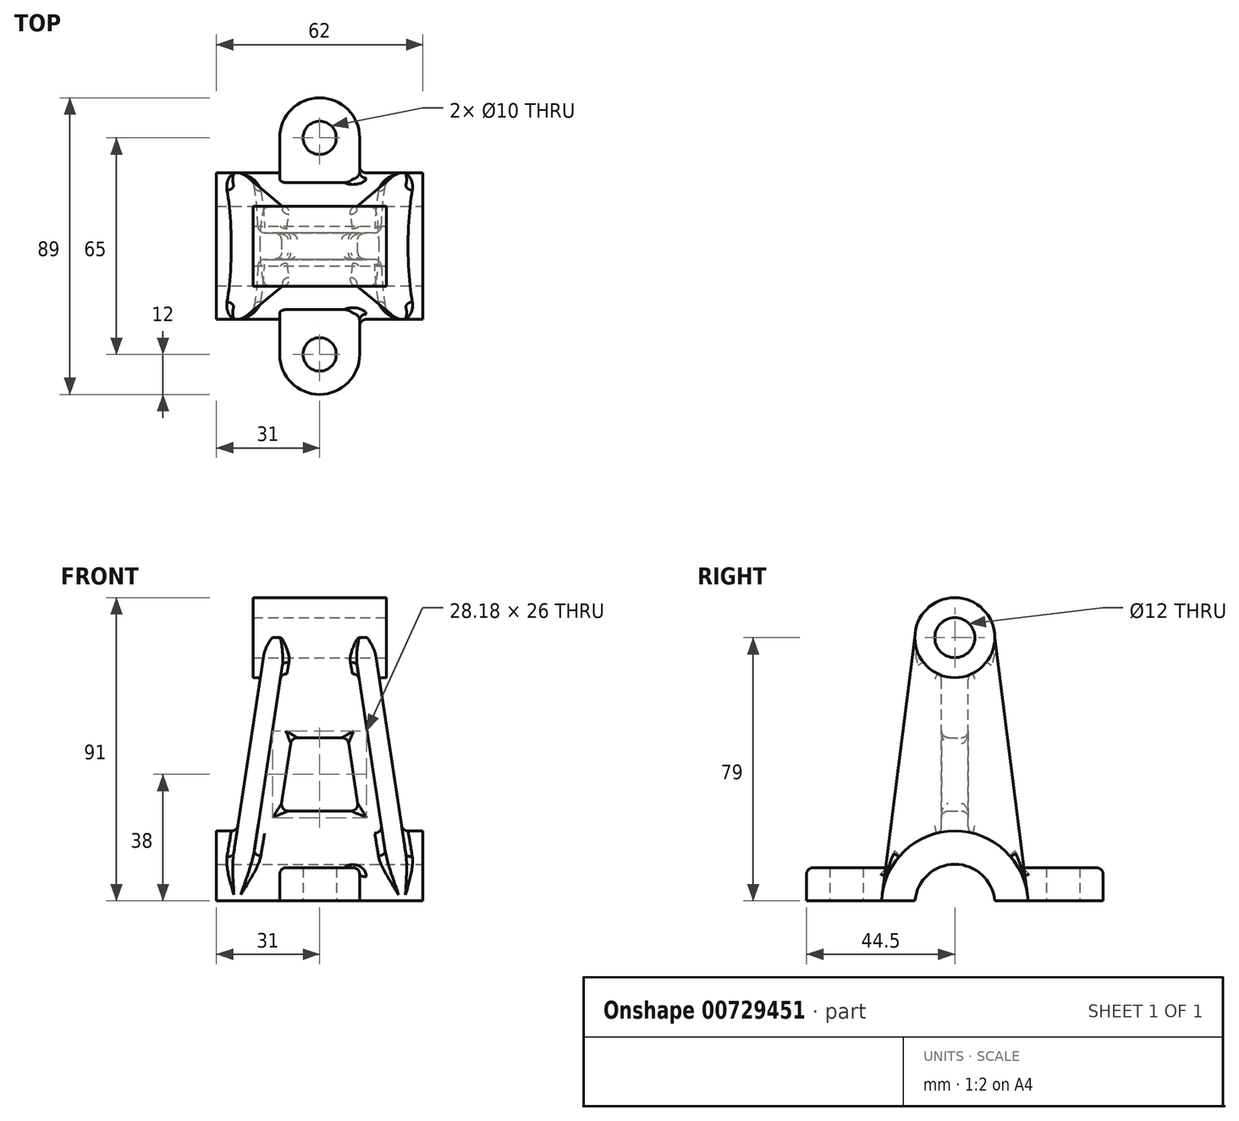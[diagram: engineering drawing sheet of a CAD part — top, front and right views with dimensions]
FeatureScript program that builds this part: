
annotation { "Feature Type Name" : "Feature", "Feature Type Description" : "" }
export const myFeature = defineFeature(function(context is Context, id is Id, definition is map)
    precondition{}
    {
        {
            var Q0;
            Q0=qCreatedBy(makeId("Right.planeOp"),FACE);
            var sketch = newSketch(context, id + "F0", { "sketchPlane" : qUnion([Q0])});
            skArc(sketch, "E0", {"start": v(21.98, 1) * mm, "mid": v(0, 22) * mm, "end": v(-21.98, 1) * mm});
            skArc(sketch, "E1", {"start": v(11.96, 1) * mm, "mid": v(0, 12) * mm, "end": v(-11.96, 1) * mm});
            skLineSegment(sketch, "E2", {"start": v(0, 0) * mm, "end": v(36.01, 0) * mm, "construction": true});
            skLineSegment(sketch, "E3", {"start": v(-21.98, 1) * mm, "end": v(21.98, 1) * mm});
            skSolve(sketch);
        }
        {
            var Q0;
            Q0 = qSketchRegion(id + "F0", true);
            extrude(context, id + "F1", {"entities" : qUnion([Q0]), "depth" : 62 * mm, "offsetDistance" : 25 * mm, "symmetric" : true});
        }
        {
            var Q0;
            Q0=qCreatedBy(makeId("Right.planeOp"),FACE);
            var sketch = newSketch(context, id + "F2", { "sketchPlane" : qUnion([Q0])});
            skLineSegment(sketch, "E4", {"start": v(0, 0) * mm, "end": v(0, 80) * mm, "construction": true});
            skCircle(sketch, "E5", {"center": v(0, 80) * mm, "radius": 6 * mm});
            skCircle(sketch, "E6", {"center": v(0, 80) * mm, "radius": 12 * mm});
            skSolve(sketch);
        }
        {
            var Q0;
            Q0 = qSketchRegion(id + "F2", true);
            var Q1;
            Q1=makeQuery(id+"F2.imprint","IMPRINT",FACE,{"disambiguationData":[TD([[makeQuery(id+"F2.imprint","IMPRINT",EDGE,{"derivedFrom":sQuery(id+"F2.wireOp",EDGE,"E5")}),1.0]])]});
            extrude(context, id + "F3", {"entities" : qUnion([Q0, Q1]), "depth" : 40 * mm, "offsetDistance" : 25 * mm, "symmetric" : true});
        }
        {
            var Q0;
            Q0=qCreatedBy(makeId("Front.planeOp"),FACE);
            var sketch = newSketch(context, id + "F4", { "sketchPlane" : qUnion([Q0])});
            skLineSegment(sketch, "E7", {"start": v(0, 0) * mm, "end": v(0, 29.66) * mm, "construction": true});
            skLineSegment(sketch, "E8", {"start": v(-16, 80) * mm, "end": v(16, 80) * mm});
            skLineSegment(sketch, "E9.0", {"start": v(28, 1) * mm, "end": v(-28, 1) * mm});
            skLineSegment(sketch, "E10", {"start": v(16, 80) * mm, "end": v(28, 1) * mm});
            skLineSegment(sketch, "E11.MirrorCS", {"start": v(-16, 80) * mm, "end": v(-28, 1) * mm});
            skLineSegment(sketch, "E12", {"start": v(-24.81, 22) * mm, "end": v(24.81, 22) * mm});
            skLineSegment(sketch, "E13.0", {"start": v(8.42, 50) * mm, "end": v(11.76, 28) * mm});
            skLineSegment(sketch, "E14.MirrorCS", {"start": v(-8.42, 50) * mm, "end": v(-11.76, 28) * mm});
            skLineSegment(sketch, "E15.trimOffspring", {"start": v(-8.42, 50) * mm, "end": v(8.42, 50) * mm});
            skLineSegment(sketch, "E16.trimOffspring", {"start": v(-11.76, 28) * mm, "end": v(11.76, 28) * mm});
            skPoint(sketch, "E17.orphan", {"position": v(-31, 1) * mm});
            skPoint(sketch, "E18.orphan", {"position": v(31, 1) * mm});
            skLineSegment(sketch, "E19", {"start": v(9.93, 80) * mm, "end": v(21.93, 1) * mm});
            skLineSegment(sketch, "E20.MirrorCS", {"start": v(-9.93, 80) * mm, "end": v(-21.93, 1) * mm});
            skSolve(sketch);
        }
        {
            var Q0;
            Q0 = qSketchRegion(id + "F4", true);
            extrude(context, id + "F5", {"entities" : qUnion([Q0]), "operationType" : NewBodyOperationType.ADD, "depth" : 8 * mm, "offsetDistance" : 25 * mm, "symmetric" : true});
        }
        {
            var Q0;
            {var subQ0=sQuery(id+"F4.wireOp",EDGE,"E10");var subQ1=sQuery(id+"F4.wireOp",EDGE,"E8");var subQ2=makeQuery(id+"F4.imprint","INTERSECT",VERTEX,{"derivedFrom":[subQ1,subQ0]});Q0=makeQuery(id+"F4.imprint","IMPRINT",FACE,{"disambiguationData":[TD([[makeQuery(id+"F4.imprint","IMPRINT",EDGE,{"disambiguationData":[TD([[subQ2,1.0]])],"derivedFrom":subQ1}),-1.0]])]});}
            var Q1;
            {var subQ0=sQuery(id+"F4.wireOp",EDGE,"E11.MirrorCS");var subQ1=sQuery(id+"F4.wireOp",EDGE,"E8");var subQ2=makeQuery(id+"F4.imprint","INTERSECT",VERTEX,{"derivedFrom":[subQ1,subQ0]});Q1=makeQuery(id+"F4.imprint","IMPRINT",FACE,{"disambiguationData":[TD([[makeQuery(id+"F4.imprint","IMPRINT",EDGE,{"disambiguationData":[TD([[subQ2,-1.0]])],"derivedFrom":subQ1}),-1.0]])]});}
            var Q2;
            {var subQ0=sQuery(id+"F4.wireOp",EDGE,"E11.MirrorCS");var subQ1=sQuery(id+"F4.wireOp",EDGE,"E9.0");var subQ2=makeQuery(id+"F4.imprint","INTERSECT",VERTEX,{"derivedFrom":[subQ1,subQ0]});Q2=makeQuery(id+"F4.imprint","IMPRINT",FACE,{"disambiguationData":[TD([[makeQuery(id+"F4.imprint","IMPRINT",EDGE,{"disambiguationData":[TD([[subQ2,1.0]])],"derivedFrom":subQ1}),-1.0]])]});}
            var Q3;
            {var subQ0=sQuery(id+"F4.wireOp",EDGE,"E10");var subQ1=sQuery(id+"F4.wireOp",EDGE,"E9.0");var subQ2=makeQuery(id+"F4.imprint","INTERSECT",VERTEX,{"derivedFrom":[subQ1,subQ0]});Q3=makeQuery(id+"F4.imprint","IMPRINT",FACE,{"disambiguationData":[TD([[makeQuery(id+"F4.imprint","IMPRINT",EDGE,{"disambiguationData":[TD([[subQ2,-1.0]])],"derivedFrom":subQ1}),-1.0]])]});}
            var Q4;
            {var subQ0=sQuery(id+"F0.wireOp",EDGE,"E3");var subQ1=sQuery(id+"F0.wireOp",EDGE,"E0");Q4=makeQuery(id+"F1.opExtrude","CAP_VERTEX",VERTEX,{"disambiguationData":[OSD([subQ1,subQ0]),TDD([makeQuery(id+"F0.imprint","INTERSECT",VERTEX,{"disambiguationData":[OD(1.0)],"derivedFrom":[subQ1,subQ0]})])],"isStart":false});}
            extrude(context, id + "F6", {"entities" : qUnion([Q0, Q1, Q2, Q3]), "operationType" : NewBodyOperationType.ADD, "endBound" : BoundingType.UP_TO_VERTEX, "depth" : 25 * mm, "endBoundEntityVertex" : qUnion([Q4]), "offsetDistance" : 25 * mm});
        }
        {
            var Q0;
            Q0=qCreatedBy(makeId("Right.planeOp"),FACE);
            var sketch = newSketch(context, id + "F7", { "sketchPlane" : qUnion([Q0])});
            skCircle(sketch, "E21.0", {"center": v(0, 80) * mm, "radius": 12 * mm});
            skArc(sketch, "E22.0", {"start": v(21.98, 1) * mm, "mid": v(0, 22) * mm, "end": v(-21.98, 1) * mm});
            skLineSegment(sketch, "E23.0", {"start": v(-21.98, 80) * mm, "end": v(-12, 80) * mm});
            skLineSegment(sketch, "E24", {"start": v(-12, 80) * mm, "end": v(-21.82, 2.78) * mm});
            skLineSegment(sketch, "E25.0", {"start": v(-21.98, 80) * mm, "end": v(-21.98, 1) * mm});
            skSolve(sketch);
        }
        {
            var Q0;
            Q0=makeQuery(id+"F7.imprint","IMPRINT",FACE,{"disambiguationData":[TD([[makeQuery(id+"F7.imprint","IMPRINT",EDGE,{"derivedFrom":sQuery(id+"F7.wireOp",EDGE,"E23.0")}),-1.0]])]});
            extrude(context, id + "F8", {"entities" : qUnion([Q0]), "operationType" : NewBodyOperationType.REMOVE, "oppositeDirection" : true, "depth" : 62 * mm, "offsetDistance" : 25 * mm, "symmetric" : true});
        }
        {
            var Q0;
            Q0=qCreatedBy(makeId("Right.planeOp"),FACE);
            var sketch = newSketch(context, id + "F9", { "sketchPlane" : qUnion([Q0])});
            skLineSegment(sketch, "E26.bottom", {"start": v(0, 0) * mm, "end": v(47.87, 0) * mm});
            skLineSegment(sketch, "E26.top", {"start": v(0, 99.51) * mm, "end": v(47.87, 99.51) * mm});
            skLineSegment(sketch, "E26.left", {"start": v(0, 0) * mm, "end": v(0, 99.51) * mm});
            skLineSegment(sketch, "E26.right", {"start": v(47.87, 0) * mm, "end": v(47.87, 99.51) * mm});
            skSolve(sketch);
        }
        {
            var Q0;
            Q0 = qSketchRegion(id + "F9", true);
            extrude(context, id + "F10", {"entities" : qUnion([Q0]), "operationType" : NewBodyOperationType.REMOVE, "oppositeDirection" : true, "depth" : 62 * mm, "offsetDistance" : 25 * mm, "symmetric" : true});
        }
        {
            var Q0;
            Q0=makeQuery(id+"F1.opExtrude","SWEPT_BODY",BODY,{"disambiguationData":[OSD([sQuery(id+"F0.wireOp",EDGE,"E0"),sQuery(id+"F0.wireOp",EDGE,"E3")])]});
            var Q1;
            Q1=qCreatedBy(makeId("Front.planeOp"),FACE);
            mirror(context, id + "F11", {"operationType" : NewBodyOperationType.ADD, "entities" : qUnion([Q0]), "mirrorPlane" : qUnion([Q1])});
        }
        {
            var Q0;
            Q0=makeQuery(id+"F1.opExtrude","SWEPT_FACE",FACE,{"disambiguationData":[OSD([sQuery(id+"F0.wireOp",EDGE,"E3")])]});
            var sketch = newSketch(context, id + "F12", { "sketchPlane" : qUnion([Q0])});
            skLineSegment(sketch, "E27", {"start": v(0, 32.5) * mm, "end": v(0, -32.5) * mm, "construction": true});
            skLineSegment(sketch, "E28", {"start": v(0, 0) * mm, "end": v(9.46, 0) * mm, "construction": true});
            skArc(sketch, "E29.0.startCap", {"start": v(-12, 32.5) * mm, "mid": v(0, 44.5) * mm, "end": v(12, 32.5) * mm});
            skArc(sketch, "E29.0.endCap", {"start": v(12, -32.5) * mm, "mid": v(0, -44.5) * mm, "end": v(-12, -32.5) * mm});
            skLineSegment(sketch, "E29.0.left", {"start": v(12, 32.5) * mm, "end": v(12, -32.5) * mm});
            skLineSegment(sketch, "E29.0.right", {"start": v(-12, 32.5) * mm, "end": v(-12, -32.5) * mm});
            skCircle(sketch, "E30", {"center": v(0, 32.5) * mm, "radius": 5 * mm});
            skCircle(sketch, "E31", {"center": v(0, -32.5) * mm, "radius": 5 * mm});
            skSolve(sketch);
        }
        {
            var Q0;
            Q0 = qSketchRegion(id + "F12", true);
            extrude(context, id + "F13", {"entities" : qUnion([Q0]), "operationType" : NewBodyOperationType.ADD, "oppositeDirection" : true, "depth" : 10 * mm, "offsetDistance" : 25 * mm});
        }
        {
            var Q0;
            {var subQ0=sQuery(id+"F0.wireOp",EDGE,"E1");Q0=makeQuery(id+"F0.imprint","IMPRINT",FACE,{"disambiguationData":[TD([[makeQuery(id+"F0.imprint","IMPRINT",EDGE,{"derivedFrom":subQ0}),1.0]])]});}
            extrude(context, id + "F14", {"entities" : qUnion([Q0]), "operationType" : NewBodyOperationType.REMOVE, "oppositeDirection" : true, "depth" : 62 * mm, "offsetDistance" : 25 * mm, "symmetric" : true});
        }
        {
            var Q0;
            Q0=makeQuery(id+"F2.imprint","IMPRINT",FACE,{"disambiguationData":[TD([[makeQuery(id+"F2.imprint","IMPRINT",EDGE,{"derivedFrom":sQuery(id+"F2.wireOp",EDGE,"E5")}),1.0]])]});
            extrude(context, id + "F15", {"entities" : qUnion([Q0]), "operationType" : NewBodyOperationType.REMOVE, "oppositeDirection" : true, "depth" : 62 * mm, "offsetDistance" : 25 * mm, "symmetric" : true});
        }
        {
            var Q0;
            {var subQ0=sQuery(id+"F12.wireOp",EDGE,"E29.0.startCap");var subQ2=sQuery(id+"F12.wireOp",EDGE,"E29.0.left");Q0=makeQuery(id+"F13.boolean.opBoolean","SPLIT",EDGE,{"disambiguationData":[TD([makeQuery(id+"F13.opExtrude","SWEPT_FACE",FACE,{"disambiguationData":[OSD([subQ0])]})])],"derivedFrom":makeQuery(id+"F13.opExtrude","CAP_EDGE",EDGE,{"disambiguationData":[OSD([subQ2])],"isStart":false})});}
            var Q1;
            {var subQ5=sQuery(id+"F4.wireOp",EDGE,"E10");var subQ13=sQuery(id+"F0.wireOp",EDGE,"E0");var subQ14=makeQuery(id+"F1.opExtrude","SWEPT_FACE",FACE,{"disambiguationData":[OSD([subQ13])]});var subQ15=makeQuery(id+"F8.boolean.opBoolean","MERGE",FACE,{"derivedFrom":[makeQuery(id+"F6.boolean.opBoolean","SPLIT",FACE,{"disambiguationData":[TD([makeQuery(id+"F5.opExtrude","SWEPT_FACE",FACE,{"disambiguationData":[OSD([subQ5])]})])],"derivedFrom":subQ14}),makeQuery(id+"F6.boolean.opBoolean","SPLIT",FACE,{"disambiguationData":[TD([makeQuery(id+"F6.opExtrude","SWEPT_FACE",FACE,{"disambiguationData":[OSD([sQuery(id+"F4.wireOp",EDGE,"E19")])]})])],"derivedFrom":subQ14}),makeQuery(id+"F8.opExtrude","SWEPT_FACE",FACE,{"disambiguationData":[OSD([sQuery(id+"F7.wireOp",EDGE,"E22.0")])]})]});Q1=makeQuery(id+"F13.boolean.opBoolean","INTERSECT",EDGE,{"disambiguationData":[OD(0.0)],"derivedFrom":[makeQuery(id+"F11.boolean.opBoolean","MERGE",FACE,{"derivedFrom":[subQ15,makeQuery(id+"F11.opPattern","COPY",FACE,{"derivedFrom":subQ15,"instanceName":"1"})]}),makeQuery(id+"F13.opExtrude","SWEPT_FACE",FACE,{"disambiguationData":[OSD([sQuery(id+"F12.wireOp",EDGE,"E29.0.left")])]})]});}
            var Q2;
            {var subQ0=sQuery(id+"F4.wireOp",EDGE,"E10");Q2=makeQuery(id+"F8.boolean.opBoolean","INTERSECT",EDGE,{"derivedFrom":[makeQuery(id+"F6.boolean.opBoolean","MERGE",FACE,{"derivedFrom":[makeQuery(id+"F5.opExtrude","SWEPT_FACE",FACE,{"disambiguationData":[OSD([subQ0])]}),makeQuery(id+"F6.opExtrude","SWEPT_FACE",FACE,{"disambiguationData":[OSD([subQ0])]})]}),makeQuery(id+"F8.opExtrude","SWEPT_FACE",FACE,{"disambiguationData":[OSD([sQuery(id+"F7.wireOp",EDGE,"E24")])]})]});}
            var Q3;
            Q3=makeQuery(id+"F8.boolean.opBoolean","INTERSECT",EDGE,{"derivedFrom":[makeQuery(id+"F6.opExtrude","SWEPT_FACE",FACE,{"disambiguationData":[OSD([sQuery(id+"F4.wireOp",EDGE,"E19")])]}),makeQuery(id+"F8.opExtrude","SWEPT_FACE",FACE,{"disambiguationData":[OSD([sQuery(id+"F7.wireOp",EDGE,"E24")])]})]});
            var Q4;
            {var subQ0=sQuery(id+"F4.wireOp",EDGE,"E11.MirrorCS");Q4=makeQuery(id+"F8.boolean.opBoolean","INTERSECT",EDGE,{"derivedFrom":[makeQuery(id+"F6.boolean.opBoolean","MERGE",FACE,{"derivedFrom":[makeQuery(id+"F5.opExtrude","SWEPT_FACE",FACE,{"disambiguationData":[OSD([subQ0])]}),makeQuery(id+"F6.opExtrude","SWEPT_FACE",FACE,{"disambiguationData":[OSD([subQ0])]})]}),makeQuery(id+"F8.opExtrude","SWEPT_FACE",FACE,{"disambiguationData":[OSD([sQuery(id+"F7.wireOp",EDGE,"E24")])]})]});}
            var Q5;
            Q5=makeQuery(id+"F8.boolean.opBoolean","INTERSECT",EDGE,{"derivedFrom":[makeQuery(id+"F6.opExtrude","SWEPT_FACE",FACE,{"disambiguationData":[OSD([sQuery(id+"F4.wireOp",EDGE,"E20.MirrorCS")])]}),makeQuery(id+"F8.opExtrude","SWEPT_FACE",FACE,{"disambiguationData":[OSD([sQuery(id+"F7.wireOp",EDGE,"E24")])]})]});
            var Q6;
            Q6=makeQuery(id+"F6.boolean.opBoolean","INTERSECT",EDGE,{"derivedFrom":[makeQuery(id+"F3.opExtrude","SWEPT_FACE",FACE,{"disambiguationData":[OSD([sQuery(id+"F2.wireOp",EDGE,"E6")])]}),makeQuery(id+"F6.opExtrude","SWEPT_FACE",FACE,{"disambiguationData":[OSD([sQuery(id+"F4.wireOp",EDGE,"E20.MirrorCS")])]})]});
            var Q7;
            Q7=makeQuery(id+"F6.boolean.opBoolean","INTERSECT",EDGE,{"derivedFrom":[makeQuery(id+"F1.opExtrude","SWEPT_FACE",FACE,{"disambiguationData":[OSD([sQuery(id+"F0.wireOp",EDGE,"E0")])]}),makeQuery(id+"F6.opExtrude","SWEPT_FACE",FACE,{"disambiguationData":[OSD([sQuery(id+"F4.wireOp",EDGE,"E20.MirrorCS")])]})]});
            var Q8;
            Q8=makeQuery(id+"F6.boolean.opBoolean","INTERSECT",EDGE,{"derivedFrom":[makeQuery(id+"F1.opExtrude","SWEPT_FACE",FACE,{"disambiguationData":[OSD([sQuery(id+"F0.wireOp",EDGE,"E0")])]}),makeQuery(id+"F6.opExtrude","SWEPT_FACE",FACE,{"disambiguationData":[OSD([sQuery(id+"F4.wireOp",EDGE,"E19")])]})]});
            var Q9;
            Q9=makeQuery(id+"F6.boolean.opBoolean","INTERSECT",EDGE,{"derivedFrom":[makeQuery(id+"F3.opExtrude","SWEPT_FACE",FACE,{"disambiguationData":[OSD([sQuery(id+"F2.wireOp",EDGE,"E6")])]}),makeQuery(id+"F6.opExtrude","SWEPT_FACE",FACE,{"disambiguationData":[OSD([sQuery(id+"F4.wireOp",EDGE,"E19")])]})]});
            var Q10;
            Q10=makeQuery(id+"F6.boolean.opBoolean","INTERSECT",EDGE,{"derivedFrom":[makeQuery(id+"F5.opExtrude","CAP_FACE",FACE,{"disambiguationData":[OSD([sQuery(id+"F4.wireOp",EDGE,"E8"),sQuery(id+"F4.wireOp",EDGE,"E9.0"),sQuery(id+"F4.wireOp",EDGE,"E10"),sQuery(id+"F4.wireOp",EDGE,"E11.MirrorCS"),sQuery(id+"F4.wireOp",EDGE,"E13.0"),sQuery(id+"F4.wireOp",EDGE,"E14.MirrorCS"),sQuery(id+"F4.wireOp",EDGE,"E15.trimOffspring"),sQuery(id+"F4.wireOp",EDGE,"E16.trimOffspring")])],"isStart":false}),makeQuery(id+"F6.opExtrude","SWEPT_FACE",FACE,{"disambiguationData":[OSD([sQuery(id+"F4.wireOp",EDGE,"E20.MirrorCS")])]})]});
            var Q11;
            Q11=makeQuery(id+"F5.boolean.opBoolean","INTERSECT",EDGE,{"derivedFrom":[makeQuery(id+"F1.opExtrude","SWEPT_FACE",FACE,{"disambiguationData":[OSD([sQuery(id+"F0.wireOp",EDGE,"E0")])]}),makeQuery(id+"F5.opExtrude","CAP_FACE",FACE,{"disambiguationData":[OSD([sQuery(id+"F4.wireOp",EDGE,"E8"),sQuery(id+"F4.wireOp",EDGE,"E9.0"),sQuery(id+"F4.wireOp",EDGE,"E10"),sQuery(id+"F4.wireOp",EDGE,"E11.MirrorCS"),sQuery(id+"F4.wireOp",EDGE,"E13.0"),sQuery(id+"F4.wireOp",EDGE,"E14.MirrorCS"),sQuery(id+"F4.wireOp",EDGE,"E15.trimOffspring"),sQuery(id+"F4.wireOp",EDGE,"E16.trimOffspring")])],"isStart":false})]});
            var Q12;
            Q12=makeQuery(id+"F6.boolean.opBoolean","INTERSECT",EDGE,{"derivedFrom":[makeQuery(id+"F5.opExtrude","CAP_FACE",FACE,{"disambiguationData":[OSD([sQuery(id+"F4.wireOp",EDGE,"E8"),sQuery(id+"F4.wireOp",EDGE,"E9.0"),sQuery(id+"F4.wireOp",EDGE,"E10"),sQuery(id+"F4.wireOp",EDGE,"E11.MirrorCS"),sQuery(id+"F4.wireOp",EDGE,"E13.0"),sQuery(id+"F4.wireOp",EDGE,"E14.MirrorCS"),sQuery(id+"F4.wireOp",EDGE,"E15.trimOffspring"),sQuery(id+"F4.wireOp",EDGE,"E16.trimOffspring")])],"isStart":false}),makeQuery(id+"F6.opExtrude","SWEPT_FACE",FACE,{"disambiguationData":[OSD([sQuery(id+"F4.wireOp",EDGE,"E19")])]})]});
            var Q13;
            Q13=makeQuery(id+"F5.boolean.opBoolean","INTERSECT",EDGE,{"derivedFrom":[makeQuery(id+"F3.opExtrude","SWEPT_FACE",FACE,{"disambiguationData":[OSD([sQuery(id+"F2.wireOp",EDGE,"E6")])]}),makeQuery(id+"F5.opExtrude","CAP_FACE",FACE,{"disambiguationData":[OSD([sQuery(id+"F4.wireOp",EDGE,"E8"),sQuery(id+"F4.wireOp",EDGE,"E9.0"),sQuery(id+"F4.wireOp",EDGE,"E10"),sQuery(id+"F4.wireOp",EDGE,"E11.MirrorCS"),sQuery(id+"F4.wireOp",EDGE,"E13.0"),sQuery(id+"F4.wireOp",EDGE,"E14.MirrorCS"),sQuery(id+"F4.wireOp",EDGE,"E15.trimOffspring"),sQuery(id+"F4.wireOp",EDGE,"E16.trimOffspring")])],"isStart":false})]});
            var Q14;
            Q14=makeQuery(id+"F5.opExtrude","CAP_EDGE",EDGE,{"disambiguationData":[OSD([sQuery(id+"F4.wireOp",EDGE,"E15.trimOffspring")])],"isStart":false});
            var Q15;
            Q15=makeQuery(id+"F5.opExtrude","CAP_EDGE",EDGE,{"disambiguationData":[OSD([sQuery(id+"F4.wireOp",EDGE,"E14.MirrorCS")])],"isStart":false});
            var Q16;
            Q16=makeQuery(id+"F5.opExtrude","CAP_EDGE",EDGE,{"disambiguationData":[OSD([sQuery(id+"F4.wireOp",EDGE,"E16.trimOffspring")])],"isStart":false});
            var Q17;
            Q17=makeQuery(id+"F5.opExtrude","CAP_EDGE",EDGE,{"disambiguationData":[OSD([sQuery(id+"F4.wireOp",EDGE,"E13.0")])],"isStart":false});
            fillet(context, id + "F16", {"entities" : qUnion([Q0, Q1, Q2, Q3, Q4, Q5, Q6, Q7, Q8, Q9, Q10, Q11, Q12, Q13, Q14, Q15, Q16, Q17]), "radius" : 2 * mm, "tangentPropagation" : true, "allowEdgeOverflow" : false});
        }
        {
            var Q0;
            Q0=qCreatedBy(makeId("Right.planeOp"),FACE);
            var sketch = newSketch(context, id + "F17", { "sketchPlane" : qUnion([Q0])});
            skLineSegment(sketch, "E32.bottom", {"start": v(0, 0) * mm, "end": v(75.65, 0) * mm});
            skLineSegment(sketch, "E32.top", {"start": v(0, 103) * mm, "end": v(75.65, 103) * mm});
            skLineSegment(sketch, "E32.left", {"start": v(0, 0) * mm, "end": v(0, 103) * mm});
            skLineSegment(sketch, "E32.right", {"start": v(75.65, 0) * mm, "end": v(75.65, 103) * mm});
            skSolve(sketch);
        }
        {
            var Q0;
            Q0=makeQuery(id+"F17.imprint","IMPRINT",FACE,{"disambiguationData":[TD([[makeQuery(id+"F17.imprint","IMPRINT",EDGE,{"derivedFrom":sQuery(id+"F17.wireOp",EDGE,"E32.bottom")}),1.0]])]});
            extrude(context, id + "F18", {"entities" : qUnion([Q0]), "operationType" : NewBodyOperationType.REMOVE, "oppositeDirection" : true, "depth" : 62 * mm, "offsetDistance" : 25 * mm, "symmetric" : true});
        }
        {
            var Q0;
            Q0=makeQuery(id+"F1.opExtrude","SWEPT_BODY",BODY,{"disambiguationData":[OSD([sQuery(id+"F0.wireOp",EDGE,"E0"),sQuery(id+"F0.wireOp",EDGE,"E3")])]});
            var Q1;
            Q1=qCreatedBy(makeId("Front.planeOp"),FACE);
            mirror(context, id + "F19", {"operationType" : NewBodyOperationType.ADD, "entities" : qUnion([Q0]), "mirrorPlane" : qUnion([Q1])});
        }
        {
            var Q0;
            {var subQ0=makeQuery(id+"F6.boolean.opBoolean","INTERSECT",EDGE,{"derivedFrom":[makeQuery(id+"F1.opExtrude","SWEPT_FACE",FACE,{"disambiguationData":[OSD([sQuery(id+"F0.wireOp",EDGE,"E0")])]}),makeQuery(id+"F6.opExtrude","SWEPT_FACE",FACE,{"disambiguationData":[OSD([sQuery(id+"F4.wireOp",EDGE,"E10")])]})]});var subQ1=makeQuery(id+"F11.boolean.opBoolean","MERGE",EDGE,{"derivedFrom":[subQ0,makeQuery(id+"F11.opPattern","COPY",EDGE,{"derivedFrom":subQ0,"instanceName":"1"})]});Q0=makeQuery(id+"F19.boolean.opBoolean","MERGE",EDGE,{"derivedFrom":[subQ1,makeQuery(id+"F19.opPattern","COPY",EDGE,{"derivedFrom":subQ1,"instanceName":"1"})]});}
            var Q1;
            {var subQ0=makeQuery(id+"F6.boolean.opBoolean","INTERSECT",EDGE,{"derivedFrom":[makeQuery(id+"F1.opExtrude","SWEPT_FACE",FACE,{"disambiguationData":[OSD([sQuery(id+"F0.wireOp",EDGE,"E0")])]}),makeQuery(id+"F6.opExtrude","SWEPT_FACE",FACE,{"disambiguationData":[OSD([sQuery(id+"F4.wireOp",EDGE,"E11.MirrorCS")])]})]});var subQ1=makeQuery(id+"F11.boolean.opBoolean","MERGE",EDGE,{"derivedFrom":[subQ0,makeQuery(id+"F11.opPattern","COPY",EDGE,{"derivedFrom":subQ0,"instanceName":"1"})]});Q1=makeQuery(id+"F19.boolean.opBoolean","MERGE",EDGE,{"derivedFrom":[subQ1,makeQuery(id+"F19.opPattern","COPY",EDGE,{"derivedFrom":subQ1,"instanceName":"1"})]});}
            var Q2;
            {var subQ0=makeQuery(id+"F5.opExtrude","SWEPT_EDGE",EDGE,{"disambiguationData":[OSD([sQuery(id+"F4.wireOp",EDGE,"E13.0"),sQuery(id+"F4.wireOp",EDGE,"E15.trimOffspring")])]});var subQ1=makeQuery(id+"F11.boolean.opBoolean","MERGE",EDGE,{"derivedFrom":[subQ0,makeQuery(id+"F11.opPattern","COPY",EDGE,{"derivedFrom":subQ0,"instanceName":"1"})]});Q2=makeQuery(id+"F19.boolean.opBoolean","MERGE",EDGE,{"derivedFrom":[subQ1,makeQuery(id+"F19.opPattern","COPY",EDGE,{"derivedFrom":subQ1,"instanceName":"1"})]});}
            var Q3;
            {var subQ0=makeQuery(id+"F5.opExtrude","SWEPT_EDGE",EDGE,{"disambiguationData":[OSD([sQuery(id+"F4.wireOp",EDGE,"E13.0"),sQuery(id+"F4.wireOp",EDGE,"E16.trimOffspring")])]});var subQ1=makeQuery(id+"F11.boolean.opBoolean","MERGE",EDGE,{"derivedFrom":[subQ0,makeQuery(id+"F11.opPattern","COPY",EDGE,{"derivedFrom":subQ0,"instanceName":"1"})]});Q3=makeQuery(id+"F19.boolean.opBoolean","MERGE",EDGE,{"derivedFrom":[subQ1,makeQuery(id+"F19.opPattern","COPY",EDGE,{"derivedFrom":subQ1,"instanceName":"1"})]});}
            var Q4;
            {var subQ0=makeQuery(id+"F5.opExtrude","SWEPT_EDGE",EDGE,{"disambiguationData":[OSD([sQuery(id+"F4.wireOp",EDGE,"E14.MirrorCS"),sQuery(id+"F4.wireOp",EDGE,"E16.trimOffspring")])]});var subQ1=makeQuery(id+"F11.boolean.opBoolean","MERGE",EDGE,{"derivedFrom":[subQ0,makeQuery(id+"F11.opPattern","COPY",EDGE,{"derivedFrom":subQ0,"instanceName":"1"})]});Q4=makeQuery(id+"F19.boolean.opBoolean","MERGE",EDGE,{"derivedFrom":[subQ1,makeQuery(id+"F19.opPattern","COPY",EDGE,{"derivedFrom":subQ1,"instanceName":"1"})]});}
            var Q5;
            {var subQ0=makeQuery(id+"F5.opExtrude","SWEPT_EDGE",EDGE,{"disambiguationData":[OSD([sQuery(id+"F4.wireOp",EDGE,"E14.MirrorCS"),sQuery(id+"F4.wireOp",EDGE,"E15.trimOffspring")])]});var subQ1=makeQuery(id+"F11.boolean.opBoolean","MERGE",EDGE,{"derivedFrom":[subQ0,makeQuery(id+"F11.opPattern","COPY",EDGE,{"derivedFrom":subQ0,"instanceName":"1"})]});Q5=makeQuery(id+"F19.boolean.opBoolean","MERGE",EDGE,{"derivedFrom":[subQ1,makeQuery(id+"F19.opPattern","COPY",EDGE,{"derivedFrom":subQ1,"instanceName":"1"})]});}
            fillet(context, id + "F20", {"entities" : qUnion([Q0, Q1, Q2, Q3, Q4, Q5]), "radius" : 2 * mm, "tangentPropagation" : true, "allowEdgeOverflow" : false});
        }
    });
